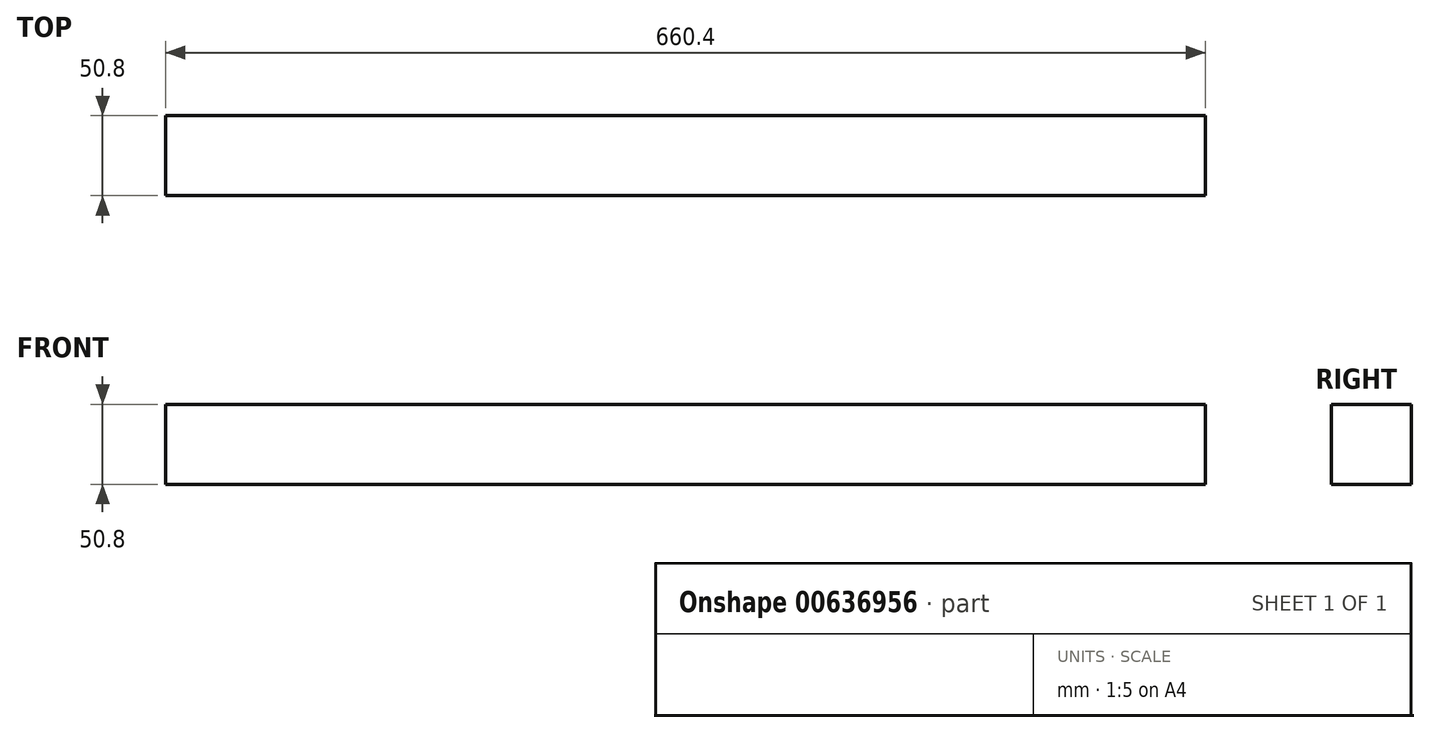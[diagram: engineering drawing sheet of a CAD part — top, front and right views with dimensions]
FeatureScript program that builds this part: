
annotation { "Feature Type Name" : "Feature", "Feature Type Description" : "" }
export const myFeature = defineFeature(function(context is Context, id is Id, definition is map)
    precondition{}
    {
        {
            var Q0;
            Q0=qCreatedBy(makeId("Top.planeOp"),FACE);
            var sketch = newSketch(context, id + "F0", { "sketchPlane" : qUnion([Q0])});
            skLineSegment(sketch, "E0.bottom", {"start": v(502.84, -23.4) * mm, "end": v(-182.96, -23.4) * mm});
            skLineSegment(sketch, "E0.top", {"start": v(502.84, 27.4) * mm, "end": v(-182.96, 27.4) * mm});
            skLineSegment(sketch, "E0.left", {"start": v(502.84, -23.4) * mm, "end": v(502.84, 27.4) * mm});
            skLineSegment(sketch, "E0.right", {"start": v(-182.96, -23.4) * mm, "end": v(-182.96, 27.4) * mm});
            skPoint(sketch, "E0.middle", {"position": v(159.94, 2) * mm});
            skSolve(sketch);
        }
        {
            var Q0;
            Q0 = qSketchRegion(id + "F0", true);
            extrude(context, id + "F1", {"entities" : qUnion([Q0]), "depth" : 50.8 * mm, "offsetDistance" : 25.4 * mm});
        }
        {
            var Q0;
            Q0=makeQuery(id+"F1.opExtrude","SWEPT_FACE",FACE,{"disambiguationData":[OSD([sQuery(id+"F0.wireOp",EDGE,"E0.right")])]});
            extrude(context, id + "F2", {"entities" : qUnion([Q0]), "operationType" : NewBodyOperationType.REMOVE, "oppositeDirection" : true, "depth" : 25.4 * mm, "offsetDistance" : 25.4 * mm});
        }
    });
